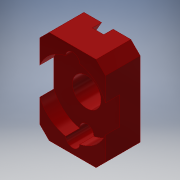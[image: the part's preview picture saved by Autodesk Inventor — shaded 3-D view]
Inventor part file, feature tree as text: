
AUTODESK INVENTOR PART (.ipt)
format: ipt  version: 2019 (Build 230136000, 136)  size: 195,072 bytes
history: native  units: mm
features: extrude x5, sketch x5, reference x5, other x5, pattern_circular x1, mirror x1, chamfer x1, projected_geometry x1
ambient origin geometry x8: Origin, YZ Plane, XZ Plane, XY Plane, X Axis, Y Axis, Z Axis, Center Point
bodies: Solid1 (feature_tree)
feature tree (24):
  extrude  "Extrusion1"  Depth=14.0mm
  extrude  "Extrusion2"  Depth=4.4mm TaperAngle=0.0deg
  extrude  "Extrusion4"  Depth=3.0mm TaperAngle=0.0deg
  extrude  "Extrusion3"  Depth=2.0mm TaperAngle=0.0deg
  extrude  "Extrusion5"  Depth=2.0mm TaperAngle=0.0deg
  pattern_circular  "Circular Pattern1"  [2 undecoded]
  mirror  "Mirror1"
  chamfer  "Chamfer1"  Distance=0.366606mm
  sketch  "Sketch1"  dims[d0=20.0mm d1=14.0mm]
  sketch  "Sketch2"  dims[d2=6.1mm d3=4.4mm d4=0.0mm]
  reference  "Reference1"
  projected_geometry  "Projected Loop1"
  sketch  "Sketch3"  dims[d5=15.2mm d6=3.0mm d7=0.0mm]
  reference  "Reference2"
  reference  "Reference3"
  sketch  "Sketch4"  dims[d8=4.77mm d9=2.0mm d10=0.0mm]
  reference  "Reference4"
  reference  "Reference5"
  sketch  "Sketch5"  dims[d11=3.0mm d12=5.0mm d13=0.0mm d15=0.62mm d16=0.366606mm d17=3.0mm d18=0.0mm d19=40.0mm d20=180.0deg d22=2.0mm d23=2.0mm d24=45.0deg]
  parser-record x1  (decoder bookkeeping rows leaked as tree rows — omitted from the tree; the rows remain in map.json)
  other  "Kinematics.iam"
  other  "Motor-GM15BY:2"
  other  "Motor-Body:1"
  other  "Mini-Q Ball caster:1"
note: 2 required parameter values undecoded (feature->parameter linkage not recoverable at this tier; creation-order binding heuristic only, values carry confidence <= 0.55)
note: 1 file-system path scrubbed to <path> (originals preserved in map.json)
